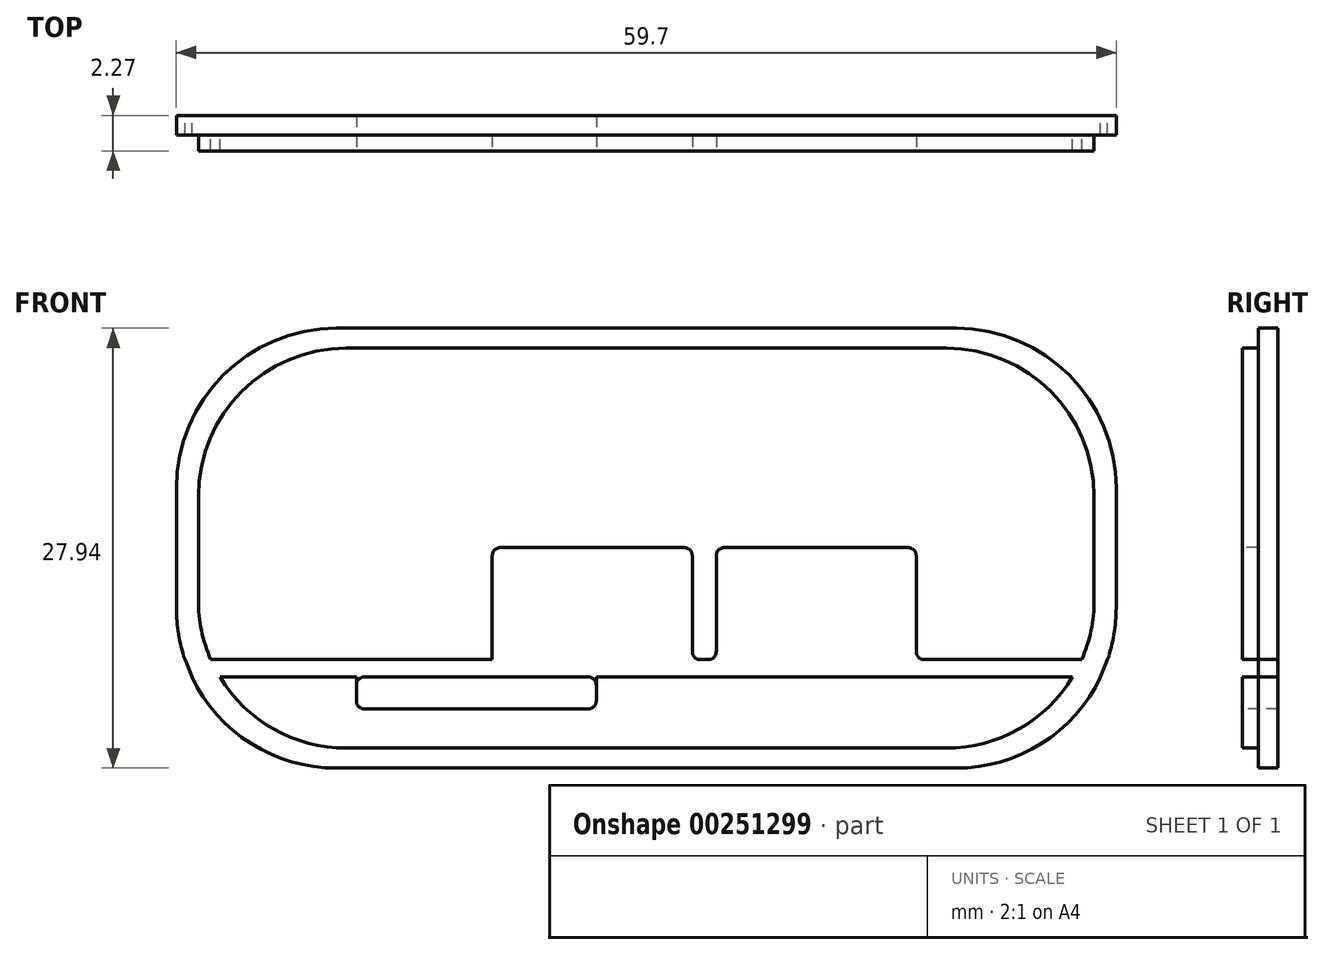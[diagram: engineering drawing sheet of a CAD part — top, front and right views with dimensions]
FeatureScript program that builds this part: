
annotation { "Feature Type Name" : "Feature", "Feature Type Description" : "" }
export const myFeature = defineFeature(function(context is Context, id is Id, definition is map)
    precondition{}
    {
        {
            var Q0;
            Q0=qCreatedBy(makeId("Front.planeOp"),FACE);
            var sketch = newSketch(context, id + "F0", { "sketchPlane" : qUnion([Q0])});
            skLineSegment(sketch, "E0.bottom", {"start": v(19.69, -13.97) * mm, "end": v(-19.69, -13.97) * mm});
            skLineSegment(sketch, "E0.top", {"start": v(19.69, 13.97) * mm, "end": v(-19.69, 13.97) * mm});
            skLineSegment(sketch, "E0.left", {"start": v(29.85, -3.81) * mm, "end": v(29.85, 3.81) * mm});
            skLineSegment(sketch, "E0.right", {"start": v(-29.85, -3.81) * mm, "end": v(-29.85, 3.8) * mm});
            skPoint(sketch, "E0.middle", {"position": v(0, 0) * mm});
            skPoint(sketch, "E1.visualSharp", {"position": v(-29.85, 13.97) * mm});
            skArc(sketch, "E1.filletArc", {"start": v(-19.69, 13.97) * mm, "mid": v(-26.87, 11) * mm, "end": v(-29.85, 3.8) * mm});
            skPoint(sketch, "E2.visualSharp", {"position": v(-29.84, -13.97) * mm});
            skArc(sketch, "E2.filletArc", {"start": v(-29.85, -3.81) * mm, "mid": v(-26.87, -11) * mm, "end": v(-19.69, -13.97) * mm});
            skPoint(sketch, "E3.visualSharp", {"position": v(29.85, -13.97) * mm});
            skArc(sketch, "E3.filletArc", {"start": v(19.69, -13.97) * mm, "mid": v(26.87, -11) * mm, "end": v(29.85, -3.81) * mm});
            skPoint(sketch, "E4.visualSharp", {"position": v(29.85, 13.97) * mm});
            skArc(sketch, "E4.filletArc", {"start": v(29.85, 3.81) * mm, "mid": v(26.87, 11) * mm, "end": v(19.69, 13.97) * mm});
            skLineSegment(sketch, "E5", {"start": v(-29.3, -7.08) * mm, "end": v(29.3, -7.08) * mm});
            skLineSegment(sketch, "E6", {"start": v(29.3, -7.08) * mm, "end": v(28.86, -8.18) * mm});
            skLineSegment(sketch, "E7", {"start": v(28.86, -8.18) * mm, "end": v(-28.86, -8.18) * mm});
            skLineSegment(sketch, "E8", {"start": v(-28.86, -8.18) * mm, "end": v(-29.3, -7.08) * mm});
            skLineSegment(sketch, "E9.bottom", {"start": v(19.05, -12.7) * mm, "end": v(-19.05, -12.7) * mm});
            skLineSegment(sketch, "E9.top", {"start": v(19.05, 12.7) * mm, "end": v(-19.05, 12.7) * mm});
            skLineSegment(sketch, "E9.left", {"start": v(28.45, -3.3) * mm, "end": v(28.45, 3.3) * mm});
            skLineSegment(sketch, "E9.right", {"start": v(-28.45, -3.3) * mm, "end": v(-28.45, 3.3) * mm});
            skPoint(sketch, "E10.visualSharp", {"position": v(-28.45, 12.7) * mm});
            skArc(sketch, "E10.filletArc", {"start": v(-19.05, 12.7) * mm, "mid": v(-25.7, 9.95) * mm, "end": v(-28.45, 3.3) * mm});
            skPoint(sketch, "E11.visualSharp", {"position": v(-28.45, -12.7) * mm});
            skArc(sketch, "E11.filletArc", {"start": v(-28.45, -3.3) * mm, "mid": v(-25.7, -9.95) * mm, "end": v(-19.05, -12.7) * mm});
            skPoint(sketch, "E12.visualSharp", {"position": v(28.45, -12.7) * mm});
            skArc(sketch, "E12.filletArc", {"start": v(19.05, -12.7) * mm, "mid": v(25.7, -9.95) * mm, "end": v(28.45, -3.3) * mm});
            skPoint(sketch, "E13.visualSharp", {"position": v(28.45, 12.7) * mm});
            skArc(sketch, "E13.filletArc", {"start": v(28.45, 3.3) * mm, "mid": v(25.7, 9.95) * mm, "end": v(19.05, 12.7) * mm});
            skSolve(sketch);
        }
        {
            var Q0;
            Q0=makeQuery(id+"F0.imprint","IMPRINT",FACE,{"disambiguationData":[TD([[makeQuery(id+"F0.imprint","IMPRINT",EDGE,{"derivedFrom":sQuery(id+"F0.wireOp",EDGE,"E0.top")}),1.0]])]});
            var Q1;
            {var subQ1=sQuery(id+"F0.wireOp",EDGE,"E0.bottom");Q1=makeQuery(id+"F0.imprint","IMPRINT",FACE,{"disambiguationData":[TD([[makeQuery(id+"F0.imprint","IMPRINT",EDGE,{"derivedFrom":subQ1}),-1.0]])]});}
            var Q2;
            {var subQ0=sQuery(id+"F0.wireOp",EDGE,"E8");Q2=makeQuery(id+"F0.imprint","IMPRINT",FACE,{"disambiguationData":[TD([[makeQuery(id+"F0.imprint","IMPRINT",EDGE,{"derivedFrom":subQ0}),-1.0]])]});}
            var Q3;
            {var subQ0=sQuery(id+"F0.wireOp",EDGE,"E6");Q3=makeQuery(id+"F0.imprint","IMPRINT",FACE,{"disambiguationData":[TD([[makeQuery(id+"F0.imprint","IMPRINT",EDGE,{"derivedFrom":subQ0}),-1.0]])]});}
            var Q4;
            Q4=makeQuery(id+"F0.imprint","IMPRINT",FACE,{"disambiguationData":[TD([[makeQuery(id+"F0.imprint","IMPRINT",EDGE,{"derivedFrom":sQuery(id+"F0.wireOp",EDGE,"E9.top")}),1.0]])]});
            var Q5;
            {var subQ0=sQuery(id+"F0.wireOp",EDGE,"E11.filletArc");var subQ1=sQuery(id+"F0.wireOp",EDGE,"E5");var subQ2=makeQuery(id+"F0.imprint","INTERSECT",VERTEX,{"derivedFrom":[subQ1,subQ0]});Q5=makeQuery(id+"F0.imprint","IMPRINT",FACE,{"disambiguationData":[TD([[makeQuery(id+"F0.imprint","IMPRINT",EDGE,{"disambiguationData":[TD([[subQ2,-1.0]])],"derivedFrom":subQ1}),-1.0]])]});}
            var Q6;
            {var subQ5=sQuery(id+"F0.wireOp",EDGE,"E9.bottom");Q6=makeQuery(id+"F0.imprint","IMPRINT",FACE,{"disambiguationData":[TD([[makeQuery(id+"F0.imprint","IMPRINT",EDGE,{"derivedFrom":subQ5}),-1.0]])]});}
            extrude(context, id + "F1", {"entities" : qUnion([Q0, Q1, Q2, Q3, Q4, Q5, Q6]), "depth" : 1.25 * mm});
        }
        {
            var Q0;
            Q0=makeQuery(id+"F1.opExtrude","CAP_FACE",FACE,{"disambiguationData":[OSD([sQuery(id+"F0.wireOp",EDGE,"E0.bottom"),sQuery(id+"F0.wireOp",EDGE,"E0.top"),sQuery(id+"F0.wireOp",EDGE,"E0.left"),sQuery(id+"F0.wireOp",EDGE,"E0.right"),sQuery(id+"F0.wireOp",EDGE,"E1.filletArc"),sQuery(id+"F0.wireOp",EDGE,"E2.filletArc"),sQuery(id+"F0.wireOp",EDGE,"E3.filletArc"),sQuery(id+"F0.wireOp",EDGE,"E4.filletArc"),sQuery(id+"F0.wireOp",EDGE,"E6"),sQuery(id+"F0.wireOp",EDGE,"E8")])],"isStart":false});
            var sketch = newSketch(context, id + "F2", { "sketchPlane" : qUnion([Q0])});
            skLineSegment(sketch, "E14.bottom", {"start": v(19.05, -12.7) * mm, "end": v(-19.05, -12.7) * mm});
            skLineSegment(sketch, "E14.top", {"start": v(19.05, 12.7) * mm, "end": v(-19.05, 12.7) * mm});
            skLineSegment(sketch, "E14.left", {"start": v(28.45, -3.3) * mm, "end": v(28.45, 3.3) * mm});
            skLineSegment(sketch, "E14.right", {"start": v(-28.45, -3.3) * mm, "end": v(-28.45, 3.3) * mm});
            skPoint(sketch, "E14.middle", {"position": v(0, 0) * mm});
            skPoint(sketch, "E15.visualSharp", {"position": v(-28.45, 12.7) * mm});
            skArc(sketch, "E15.filletArc", {"start": v(-19.05, 12.7) * mm, "mid": v(-25.7, 9.95) * mm, "end": v(-28.45, 3.3) * mm});
            skPoint(sketch, "E16.visualSharp", {"position": v(-28.45, -12.7) * mm});
            skArc(sketch, "E16.filletArc", {"start": v(-28.45, -3.3) * mm, "mid": v(-25.7, -9.95) * mm, "end": v(-19.05, -12.7) * mm});
            skPoint(sketch, "E17.visualSharp", {"position": v(28.45, -12.7) * mm});
            skArc(sketch, "E17.filletArc", {"start": v(19.05, -12.7) * mm, "mid": v(25.7, -9.95) * mm, "end": v(28.45, -3.3) * mm});
            skPoint(sketch, "E18.visualSharp", {"position": v(28.45, 12.7) * mm});
            skArc(sketch, "E18.filletArc", {"start": v(28.45, 3.3) * mm, "mid": v(25.7, 9.95) * mm, "end": v(19.05, 12.7) * mm});
            skLineSegment(sketch, "E19", {"start": v(-27.66, -7.08) * mm, "end": v(27.66, -7.08) * mm});
            skLineSegment(sketch, "E20", {"start": v(27.66, -7.08) * mm, "end": v(27.08, -8.18) * mm});
            skLineSegment(sketch, "E21", {"start": v(27.08, -8.18) * mm, "end": v(-27.08, -8.18) * mm});
            skLineSegment(sketch, "E22", {"start": v(-27.08, -8.18) * mm, "end": v(-27.66, -7.08) * mm});
            skSolve(sketch);
        }
        {
            var Q0;
            Q0=makeQuery(id+"F2.imprint","IMPRINT",FACE,{"disambiguationData":[TD([[makeQuery(id+"F2.imprint","IMPRINT",EDGE,{"derivedFrom":sQuery(id+"F2.wireOp",EDGE,"E14.bottom")}),-1.0]])]});
            var Q1;
            Q1=makeQuery(id+"F2.imprint","IMPRINT",FACE,{"disambiguationData":[TD([[makeQuery(id+"F2.imprint","IMPRINT",EDGE,{"derivedFrom":sQuery(id+"F2.wireOp",EDGE,"E14.top")}),1.0]])]});
            extrude(context, id + "F3", {"entities" : qUnion([Q0, Q1]), "operationType" : NewBodyOperationType.ADD, "depth" : 1.02 * mm});
        }
        {
            var Q0;
            Q0=makeQuery(id+"F3.opExtrude","CAP_FACE",FACE,{"disambiguationData":[OSD([sQuery(id+"F2.wireOp",EDGE,"E14.top"),sQuery(id+"F2.wireOp",EDGE,"E14.left"),sQuery(id+"F2.wireOp",EDGE,"E14.right"),sQuery(id+"F2.wireOp",EDGE,"E15.filletArc"),sQuery(id+"F2.wireOp",EDGE,"E16.filletArc"),sQuery(id+"F2.wireOp",EDGE,"E17.filletArc"),sQuery(id+"F2.wireOp",EDGE,"E18.filletArc"),sQuery(id+"F2.wireOp",EDGE,"E19")])],"isStart":false});
            var sketch = newSketch(context, id + "F4", { "sketchPlane" : qUnion([Q0])});
            skLineSegment(sketch, "E23", {"start": v(17.14, -7.08) * mm, "end": v(17.14, 0.04) * mm});
            skLineSegment(sketch, "E24", {"start": v(17.14, 0.04) * mm, "end": v(4.44, 0.04) * mm});
            skLineSegment(sketch, "E25", {"start": v(4.44, 0.04) * mm, "end": v(4.45, -7.08) * mm});
            skLineSegment(sketch, "E26", {"start": v(2.92, -7.08) * mm, "end": v(2.92, 0.04) * mm});
            skLineSegment(sketch, "E27", {"start": v(2.92, 0.04) * mm, "end": v(-9.78, 0.04) * mm});
            skLineSegment(sketch, "E28", {"start": v(-9.78, 0.04) * mm, "end": v(-9.78, -7.08) * mm});
            skSolve(sketch);
        }
        {
            var Q0;
            {var subQ0=sQuery(id+"F4.wireOp",EDGE,"E26");Q0=makeQuery(id+"F4.imprint","IMPRINT",FACE,{"disambiguationData":[TD([[makeQuery(id+"F4.imprint","IMPRINT",EDGE,{"derivedFrom":subQ0}),1.0]])]});}
            var Q1;
            {var subQ0=sQuery(id+"F4.wireOp",EDGE,"E23");Q1=makeQuery(id+"F4.imprint","IMPRINT",FACE,{"disambiguationData":[TD([[makeQuery(id+"F4.imprint","IMPRINT",EDGE,{"derivedFrom":subQ0}),1.0]])]});}
            extrude(context, id + "F5", {"entities" : qUnion([Q0, Q1]), "operationType" : NewBodyOperationType.REMOVE, "oppositeDirection" : true, "depth" : 1.02 * mm});
        }
        {
            var Q0;
            Q0=makeQuery(id+"F3.opExtrude","CAP_FACE",FACE,{"disambiguationData":[OSD([sQuery(id+"F2.wireOp",EDGE,"E14.bottom"),sQuery(id+"F2.wireOp",EDGE,"E16.filletArc"),sQuery(id+"F2.wireOp",EDGE,"E17.filletArc"),sQuery(id+"F2.wireOp",EDGE,"E21")])],"isStart":false});
            var sketch = newSketch(context, id + "F6", { "sketchPlane" : qUnion([Q0])});
            skLineSegment(sketch, "E29", {"start": v(-18.41, -8.18) * mm, "end": v(-18.41, -10.21) * mm});
            skLineSegment(sketch, "E30", {"start": v(-18.41, -10.21) * mm, "end": v(-3.18, -10.21) * mm});
            skLineSegment(sketch, "E31", {"start": v(-3.18, -10.21) * mm, "end": v(-3.18, -8.18) * mm});
            skSolve(sketch);
        }
        {
            var Q0;
            {var subQ0=sQuery(id+"F6.wireOp",EDGE,"E29");Q0=makeQuery(id+"F6.imprint","IMPRINT",FACE,{"disambiguationData":[TD([[makeQuery(id+"F6.imprint","IMPRINT",EDGE,{"derivedFrom":subQ0}),1.0]])]});}
            extrude(context, id + "F7", {"entities" : qUnion([Q0]), "operationType" : NewBodyOperationType.REMOVE, "oppositeDirection" : true, "depth" : 25.4 * mm});
        }
        {
            var Q0;
            {var subQ0=sQuery(id+"F4.wireOp",EDGE,"E23");var subQ1=sQuery(id+"F2.wireOp",EDGE,"E19");var subQ3=sQuery(id+"F0.wireOp",EDGE,"E8");var subQ4=sQuery(id+"F0.wireOp",EDGE,"E6");var subQ5=sQuery(id+"F0.wireOp",EDGE,"E4.filletArc");var subQ6=sQuery(id+"F0.wireOp",EDGE,"E3.filletArc");var subQ7=sQuery(id+"F0.wireOp",EDGE,"E2.filletArc");var subQ8=sQuery(id+"F0.wireOp",EDGE,"E1.filletArc");var subQ9=sQuery(id+"F0.wireOp",EDGE,"E0.right");var subQ10=sQuery(id+"F0.wireOp",EDGE,"E0.left");var subQ11=sQuery(id+"F0.wireOp",EDGE,"E0.top");var subQ12=sQuery(id+"F0.wireOp",EDGE,"E0.bottom");Q0=makeQuery(id+"F5.boolean.opBoolean","COPY",EDGE,{"disambiguationData":[TD([makeQuery(id+"F1.opExtrude","CAP_FACE",FACE,{"disambiguationData":[OSD([subQ12,subQ11,subQ10,subQ9,subQ8,subQ7,subQ6,subQ5,subQ4,subQ3])],"isStart":true})])],"derivedFrom":makeQuery(id+"F5.opExtrude","SWEPT_EDGE",EDGE,{"disambiguationData":[OSD([subQ1,subQ0])]})});}
            var Q1;
            Q1=makeQuery(id+"F5.boolean.opBoolean","COPY",EDGE,{"derivedFrom":makeQuery(id+"F5.opExtrude","SWEPT_EDGE",EDGE,{"disambiguationData":[OSD([sQuery(id+"F4.wireOp",EDGE,"E23"),sQuery(id+"F4.wireOp",EDGE,"E24")])]})});
            var Q2;
            {var subQ0=sQuery(id+"F4.wireOp",EDGE,"E25");var subQ1=sQuery(id+"F2.wireOp",EDGE,"E19");var subQ3=sQuery(id+"F0.wireOp",EDGE,"E8");var subQ4=sQuery(id+"F0.wireOp",EDGE,"E6");var subQ5=sQuery(id+"F0.wireOp",EDGE,"E4.filletArc");var subQ6=sQuery(id+"F0.wireOp",EDGE,"E3.filletArc");var subQ7=sQuery(id+"F0.wireOp",EDGE,"E2.filletArc");var subQ8=sQuery(id+"F0.wireOp",EDGE,"E1.filletArc");var subQ9=sQuery(id+"F0.wireOp",EDGE,"E0.right");var subQ10=sQuery(id+"F0.wireOp",EDGE,"E0.left");var subQ11=sQuery(id+"F0.wireOp",EDGE,"E0.top");var subQ12=sQuery(id+"F0.wireOp",EDGE,"E0.bottom");Q2=makeQuery(id+"F5.boolean.opBoolean","COPY",EDGE,{"disambiguationData":[TD([makeQuery(id+"F1.opExtrude","CAP_FACE",FACE,{"disambiguationData":[OSD([subQ12,subQ11,subQ10,subQ9,subQ8,subQ7,subQ6,subQ5,subQ4,subQ3])],"isStart":true})])],"derivedFrom":makeQuery(id+"F5.opExtrude","SWEPT_EDGE",EDGE,{"disambiguationData":[OSD([subQ1,subQ0])]})});}
            var Q3;
            Q3=makeQuery(id+"F5.boolean.opBoolean","COPY",EDGE,{"derivedFrom":makeQuery(id+"F5.opExtrude","SWEPT_EDGE",EDGE,{"disambiguationData":[OSD([sQuery(id+"F4.wireOp",EDGE,"E24"),sQuery(id+"F4.wireOp",EDGE,"E25")])]})});
            var Q4;
            Q4=makeQuery(id+"F5.boolean.opBoolean","COPY",EDGE,{"derivedFrom":makeQuery(id+"F5.opExtrude","SWEPT_EDGE",EDGE,{"disambiguationData":[OSD([sQuery(id+"F4.wireOp",EDGE,"E27"),sQuery(id+"F4.wireOp",EDGE,"E28")])]})});
            var Q5;
            Q5=makeQuery(id+"F5.boolean.opBoolean","COPY",EDGE,{"derivedFrom":makeQuery(id+"F5.opExtrude","SWEPT_EDGE",EDGE,{"disambiguationData":[OSD([sQuery(id+"F4.wireOp",EDGE,"E26"),sQuery(id+"F4.wireOp",EDGE,"E27")])]})});
            var Q6;
            {var subQ0=sQuery(id+"F4.wireOp",EDGE,"E26");var subQ1=sQuery(id+"F2.wireOp",EDGE,"E19");var subQ2=sQuery(id+"F0.wireOp",EDGE,"E8");var subQ3=sQuery(id+"F0.wireOp",EDGE,"E6");var subQ4=sQuery(id+"F0.wireOp",EDGE,"E4.filletArc");var subQ5=sQuery(id+"F0.wireOp",EDGE,"E3.filletArc");var subQ6=sQuery(id+"F0.wireOp",EDGE,"E2.filletArc");var subQ7=sQuery(id+"F0.wireOp",EDGE,"E1.filletArc");var subQ8=sQuery(id+"F0.wireOp",EDGE,"E0.right");var subQ9=sQuery(id+"F0.wireOp",EDGE,"E0.left");var subQ10=sQuery(id+"F0.wireOp",EDGE,"E0.top");var subQ11=sQuery(id+"F0.wireOp",EDGE,"E0.bottom");Q6=makeQuery(id+"F5.boolean.opBoolean","COPY",EDGE,{"disambiguationData":[TD([makeQuery(id+"F1.opExtrude","CAP_FACE",FACE,{"disambiguationData":[OSD([subQ11,subQ10,subQ9,subQ8,subQ7,subQ6,subQ5,subQ4,subQ3,subQ2])],"isStart":true})])],"derivedFrom":makeQuery(id+"F5.opExtrude","SWEPT_EDGE",EDGE,{"disambiguationData":[OSD([subQ1,subQ0])]})});}
            var Q7;
            {var subQ0=sQuery(id+"F4.wireOp",EDGE,"E28");var subQ1=sQuery(id+"F2.wireOp",EDGE,"E19");var subQ2=sQuery(id+"F0.wireOp",EDGE,"E8");var subQ3=sQuery(id+"F0.wireOp",EDGE,"E6");var subQ4=sQuery(id+"F0.wireOp",EDGE,"E4.filletArc");var subQ5=sQuery(id+"F0.wireOp",EDGE,"E3.filletArc");var subQ6=sQuery(id+"F0.wireOp",EDGE,"E2.filletArc");var subQ7=sQuery(id+"F0.wireOp",EDGE,"E1.filletArc");var subQ8=sQuery(id+"F0.wireOp",EDGE,"E0.right");var subQ9=sQuery(id+"F0.wireOp",EDGE,"E0.left");var subQ10=sQuery(id+"F0.wireOp",EDGE,"E0.top");var subQ11=sQuery(id+"F0.wireOp",EDGE,"E0.bottom");Q7=makeQuery(id+"F5.boolean.opBoolean","COPY",EDGE,{"disambiguationData":[TD([makeQuery(id+"F1.opExtrude","CAP_FACE",FACE,{"disambiguationData":[OSD([subQ11,subQ10,subQ9,subQ8,subQ7,subQ6,subQ5,subQ4,subQ3,subQ2])],"isStart":true})])],"derivedFrom":makeQuery(id+"F5.opExtrude","SWEPT_EDGE",EDGE,{"disambiguationData":[OSD([subQ1,subQ0])]})});}
            var Q8;
            Q8=makeQuery(id+"F7.boolean.opBoolean","COPY",EDGE,{"derivedFrom":makeQuery(id+"F7.opExtrude","SWEPT_EDGE",EDGE,{"disambiguationData":[OSD([sQuery(id+"F6.wireOp",EDGE,"E30"),sQuery(id+"F6.wireOp",EDGE,"E31")])]})});
            var Q9;
            {var subQ0=sQuery(id+"F6.wireOp",EDGE,"E29");var subQ1=sQuery(id+"F2.wireOp",EDGE,"E21");Q9=makeQuery(id+"F7.boolean.opBoolean","COPY",EDGE,{"disambiguationData":[topologyDisambiguationEdgeConnected([makeQuery(id+"F7.opExtrude","SWEPT_FACE",FACE,{"disambiguationData":[OSD([subQ1])]})])],"derivedFrom":makeQuery(id+"F7.opExtrude","SWEPT_EDGE",EDGE,{"disambiguationData":[OSD([subQ1,subQ0])]})});}
            var Q10;
            Q10=makeQuery(id+"F7.boolean.opBoolean","COPY",EDGE,{"derivedFrom":makeQuery(id+"F7.opExtrude","SWEPT_EDGE",EDGE,{"disambiguationData":[OSD([sQuery(id+"F6.wireOp",EDGE,"E29"),sQuery(id+"F6.wireOp",EDGE,"E30")])]})});
            var Q11;
            {var subQ0=sQuery(id+"F6.wireOp",EDGE,"E31");var subQ1=sQuery(id+"F2.wireOp",EDGE,"E21");Q11=makeQuery(id+"F7.boolean.opBoolean","COPY",EDGE,{"disambiguationData":[topologyDisambiguationEdgeConnected([makeQuery(id+"F7.opExtrude","SWEPT_FACE",FACE,{"disambiguationData":[OSD([subQ1])]})])],"derivedFrom":makeQuery(id+"F7.opExtrude","SWEPT_EDGE",EDGE,{"disambiguationData":[OSD([subQ1,subQ0])]})});}
            fillet(context, id + "F8", {"entities" : qUnion([Q0, Q1, Q2, Q3, Q4, Q5, Q6, Q7, Q8, Q9, Q10, Q11]), "radius" : 0.5 * mm, "tangentPropagation" : true, "allowEdgeOverflow" : false});
        }
    });
